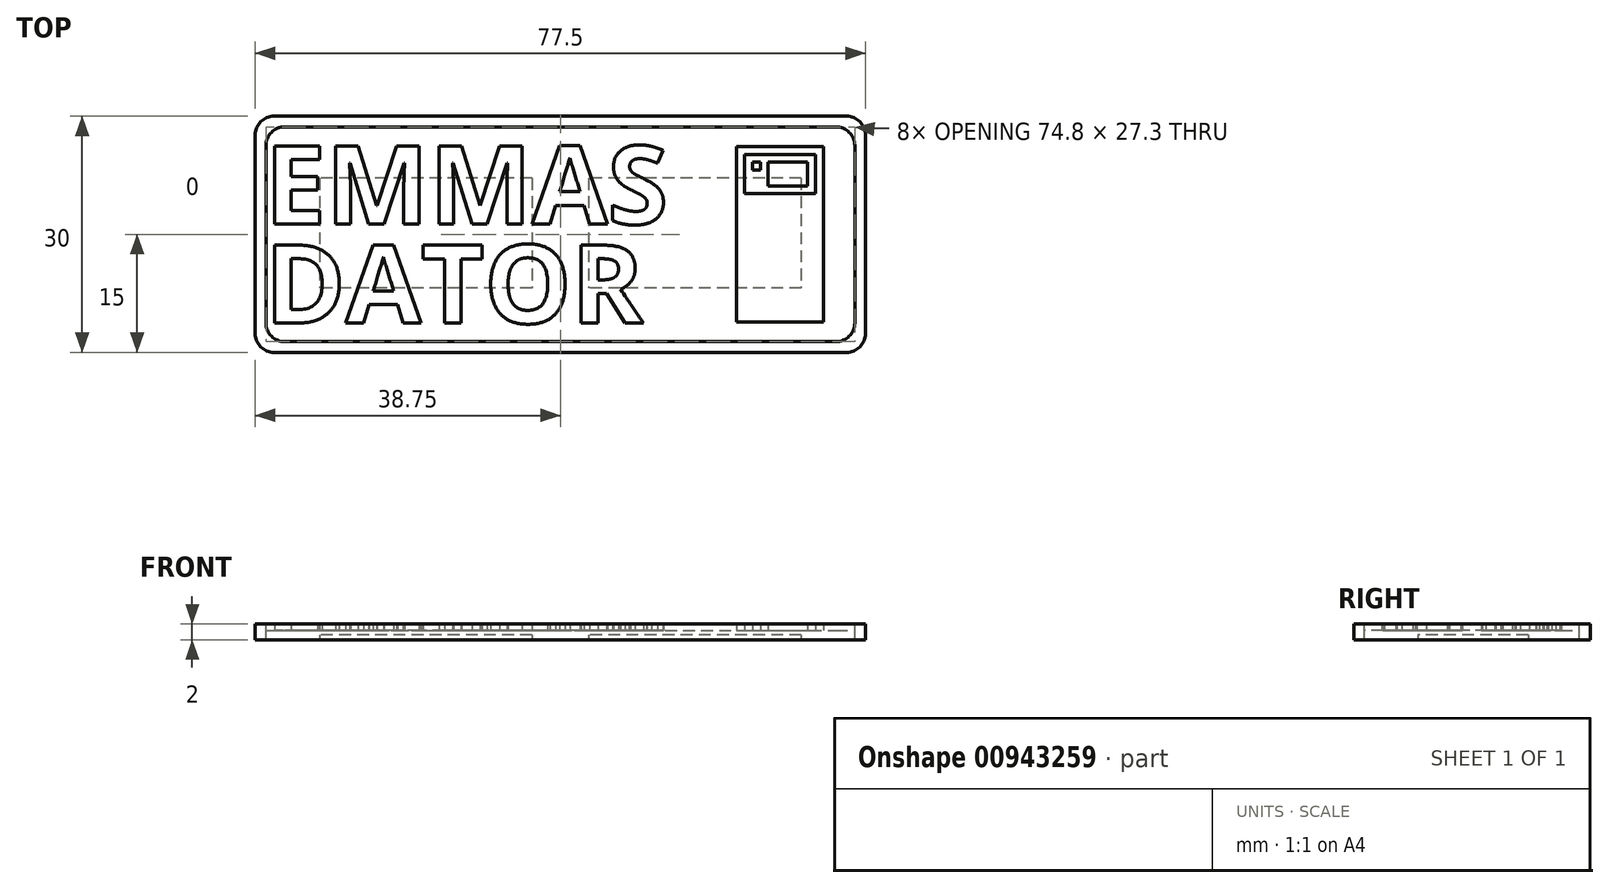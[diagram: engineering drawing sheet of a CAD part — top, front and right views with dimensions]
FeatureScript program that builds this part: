
annotation { "Feature Type Name" : "Feature", "Feature Type Description" : "" }
export const myFeature = defineFeature(function(context is Context, id is Id, definition is map)
    precondition{}
    {
        {
            var Q0;
            Q0=qCreatedBy(makeId("Top.planeOp"),FACE);
            var sketch = newSketch(context, id + "F0", { "sketchPlane" : qUnion([Q0])});
            skLineSegment(sketch, "E0.bottom", {"start": v(-77.5, 30) * mm, "end": v(0, 30) * mm});
            skLineSegment(sketch, "E0.top", {"start": v(-77.5, 0) * mm, "end": v(0, 0) * mm});
            skLineSegment(sketch, "E0.left", {"start": v(-77.5, 30) * mm, "end": v(-77.5, 0) * mm});
            skLineSegment(sketch, "E0.right", {"start": v(0, 30) * mm, "end": v(0, 0) * mm});
            skSolve(sketch);
        }
        {
            var Q0;
            Q0=makeQuery(id+"F0.imprint","IMPRINT",FACE,{"disambiguationData":[TD([[makeQuery(id+"F0.imprint","IMPRINT",EDGE,{"derivedFrom":sQuery(id+"F0.wireOp",EDGE,"E0.bottom")}),-1.0]])]});
            extrude(context, id + "F1", {"entities" : qUnion([Q0]), "oppositeDirection" : true, "depth" : 2 * mm, "offsetDistance" : 25 * mm});
        }
        {
            var Q0;
            Q0=makeQuery(id+"F1.opExtrude","CAP_FACE",FACE,{"disambiguationData":[OSD([sQuery(id+"F0.wireOp",EDGE,"E0.bottom"),sQuery(id+"F0.wireOp",EDGE,"E0.top"),sQuery(id+"F0.wireOp",EDGE,"E0.left"),sQuery(id+"F0.wireOp",EDGE,"E0.right")])],"isStart":true});
            var sketch = newSketch(context, id + "F2", { "sketchPlane" : qUnion([Q0])});
            skLineSegment(sketch, "E1.bottom", {"start": v(-76.15, 28.65) * mm, "end": v(-1.35, 28.65) * mm});
            skLineSegment(sketch, "E1.top", {"start": v(-76.15, 1.35) * mm, "end": v(-1.35, 1.35) * mm});
            skLineSegment(sketch, "E1.left", {"start": v(-76.15, 28.65) * mm, "end": v(-76.15, 1.35) * mm});
            skLineSegment(sketch, "E1.right", {"start": v(-1.35, 28.65) * mm, "end": v(-1.35, 1.35) * mm});
            skSolve(sketch);
        }
        {
            var Q0;
            Q0=makeQuery(id+"F2.imprint","IMPRINT",FACE,{"disambiguationData":[TD([[makeQuery(id+"F2.imprint","IMPRINT",EDGE,{"derivedFrom":sQuery(id+"F2.wireOp",EDGE,"E1.bottom")}),-1.0]])]});
            extrude(context, id + "F3", {"entities" : qUnion([Q0]), "operationType" : NewBodyOperationType.REMOVE, "oppositeDirection" : true, "depth" : 0.8 * mm, "offsetDistance" : 25 * mm});
        }
        {
            var Q0;
            Q0=makeQuery(id+"F1.opExtrude","SWEPT_EDGE",EDGE,{"disambiguationData":[OSD([sQuery(id+"F0.wireOp",EDGE,"E0.bottom"),sQuery(id+"F0.wireOp",EDGE,"E0.right")])]});
            var Q1;
            Q1=makeQuery(id+"F1.opExtrude","SWEPT_EDGE",EDGE,{"disambiguationData":[OSD([sQuery(id+"F0.wireOp",EDGE,"E0.top"),sQuery(id+"F0.wireOp",EDGE,"E0.right")])]});
            var Q2;
            Q2=makeQuery(id+"F1.opExtrude","SWEPT_EDGE",EDGE,{"disambiguationData":[OSD([sQuery(id+"F0.wireOp",EDGE,"E0.top"),sQuery(id+"F0.wireOp",EDGE,"E0.left")])]});
            var Q3;
            Q3=makeQuery(id+"F1.opExtrude","SWEPT_EDGE",EDGE,{"disambiguationData":[OSD([sQuery(id+"F0.wireOp",EDGE,"E0.bottom"),sQuery(id+"F0.wireOp",EDGE,"E0.left")])]});
            var Q4;
            Q4=makeQuery(id+"F3.boolean.opBoolean","COPY",EDGE,{"derivedFrom":makeQuery(id+"F3.opExtrude","SWEPT_EDGE",EDGE,{"disambiguationData":[OSD([sQuery(id+"F2.wireOp",EDGE,"E1.top"),sQuery(id+"F2.wireOp",EDGE,"E1.right")])]})});
            var Q5;
            Q5=makeQuery(id+"F3.boolean.opBoolean","COPY",EDGE,{"derivedFrom":makeQuery(id+"F3.opExtrude","SWEPT_EDGE",EDGE,{"disambiguationData":[OSD([sQuery(id+"F2.wireOp",EDGE,"E1.bottom"),sQuery(id+"F2.wireOp",EDGE,"E1.right")])]})});
            var Q6;
            Q6=makeQuery(id+"F3.boolean.opBoolean","COPY",EDGE,{"derivedFrom":makeQuery(id+"F3.opExtrude","SWEPT_EDGE",EDGE,{"disambiguationData":[OSD([sQuery(id+"F2.wireOp",EDGE,"E1.bottom"),sQuery(id+"F2.wireOp",EDGE,"E1.left")])]})});
            var Q7;
            Q7=makeQuery(id+"F3.boolean.opBoolean","COPY",EDGE,{"derivedFrom":makeQuery(id+"F3.opExtrude","SWEPT_EDGE",EDGE,{"disambiguationData":[OSD([sQuery(id+"F2.wireOp",EDGE,"E1.top"),sQuery(id+"F2.wireOp",EDGE,"E1.left")])]})});
            fillet(context, id + "F4", {"entities" : qUnion([Q0, Q1, Q2, Q3, Q4, Q5, Q6, Q7]), "radius" : 2.4 * mm, "tangentPropagation" : true, "allowEdgeOverflow" : false});
        }
        {
            var Q0;
            Q0=makeQuery(id+"F3.boolean.opBoolean","COPY",FACE,{"derivedFrom":makeQuery(id+"F3.opExtrude","CAP_FACE",FACE,{"disambiguationData":[OSD([sQuery(id+"F2.wireOp",EDGE,"E1.bottom"),sQuery(id+"F2.wireOp",EDGE,"E1.top"),sQuery(id+"F2.wireOp",EDGE,"E1.left"),sQuery(id+"F2.wireOp",EDGE,"E1.right")])],"isStart":false})});
            extrude(context, id + "F5", {"entities" : qUnion([Q0]), "oppositeDirection" : true, "depth" : 1.2 * mm, "offsetDistance" : 25 * mm});
        }
        {
            var Q0;
            Q0=makeQuery(id+"F5.opExtrude","SWEPT_BODY",BODY,{"disambiguationData":[OSD([sQuery(id+"F2.wireOp",EDGE,"E1.bottom"),sQuery(id+"F2.wireOp",EDGE,"E1.top"),sQuery(id+"F2.wireOp",EDGE,"E1.left"),sQuery(id+"F2.wireOp",EDGE,"E1.right")])]});
            var Q1;
            Q1=makeQuery(id+"F1.opExtrude","SWEPT_BODY",BODY,{"disambiguationData":[OSD([sQuery(id+"F0.wireOp",EDGE,"E0.bottom"),sQuery(id+"F0.wireOp",EDGE,"E0.top"),sQuery(id+"F0.wireOp",EDGE,"E0.left"),sQuery(id+"F0.wireOp",EDGE,"E0.right")])]});
            booleanBodies(context, id + "F6", {"operationType" : BooleanOperationType.SUBTRACTION, "tools" : qUnion([Q0]), "targets" : qUnion([Q1]), "keepTools" : true});
        }
        {
            var Q0;
            Q0=makeQuery(id+"F5.opExtrude","CAP_FACE",FACE,{"disambiguationData":[OSD([sQuery(id+"F2.wireOp",EDGE,"E1.bottom"),sQuery(id+"F2.wireOp",EDGE,"E1.top"),sQuery(id+"F2.wireOp",EDGE,"E1.left"),sQuery(id+"F2.wireOp",EDGE,"E1.right")])],"isStart":true});
            var sketch = newSketch(context, id + "F7", { "sketchPlane" : qUnion([Q0])});
            skText(sketch, "E2", { "text": "EMMAS", "fontName": "OpenSans-Bold.ttf"});
            skText(sketch, "E3", { "text": "DATOR", "fontName": "OpenSans-Bold.ttf"});
            skLineSegment(sketch, "E4.bottom", {"start": v(-16.35, 26.15) * mm, "end": v(-5.35, 26.15) * mm});
            skLineSegment(sketch, "E4.top", {"start": v(-16.35, 3.85) * mm, "end": v(-5.35, 3.85) * mm});
            skLineSegment(sketch, "E4.left", {"start": v(-16.35, 26.15) * mm, "end": v(-16.35, 3.85) * mm});
            skLineSegment(sketch, "E4.right", {"start": v(-5.35, 26.15) * mm, "end": v(-5.35, 3.85) * mm});
            skLineSegment(sketch, "E5.bottom", {"start": v(-15.35, 25.15) * mm, "end": v(-6.35, 25.15) * mm});
            skLineSegment(sketch, "E5.top", {"start": v(-15.35, 20.15) * mm, "end": v(-6.35, 20.15) * mm});
            skLineSegment(sketch, "E5.left", {"start": v(-15.35, 25.15) * mm, "end": v(-15.35, 20.15) * mm});
            skLineSegment(sketch, "E5.right", {"start": v(-6.35, 25.15) * mm, "end": v(-6.35, 20.15) * mm});
            skLineSegment(sketch, "E6.bottom", {"start": v(-14.35, 24.15) * mm, "end": v(-13.35, 24.15) * mm});
            skLineSegment(sketch, "E6.top", {"start": v(-14.35, 23.15) * mm, "end": v(-13.35, 23.15) * mm});
            skLineSegment(sketch, "E6.left", {"start": v(-14.35, 24.15) * mm, "end": v(-14.35, 23.15) * mm});
            skLineSegment(sketch, "E6.right", {"start": v(-13.35, 24.15) * mm, "end": v(-13.35, 23.15) * mm});
            skLineSegment(sketch, "E7.bottom", {"start": v(-12.35, 24.15) * mm, "end": v(-7.35, 24.15) * mm});
            skLineSegment(sketch, "E7.top", {"start": v(-12.35, 21.15) * mm, "end": v(-7.35, 21.15) * mm});
            skLineSegment(sketch, "E7.left", {"start": v(-12.35, 24.15) * mm, "end": v(-12.35, 21.15) * mm});
            skLineSegment(sketch, "E7.right", {"start": v(-7.35, 24.15) * mm, "end": v(-7.35, 21.15) * mm});
            const initialGuessF7  = {"E2": [-0.0763, 0.0163, 1, 0, 0.01], "E3": [-0.0763, 0.0037, 1, 0, 0.01]};
            skSetInitialGuess(sketch, initialGuessF7);
            skSolve(sketch);
        }
        {
            var Q0;
            Q0 = qSketchRegion(id + "F7", true);
            var Q1;
            Q1=makeQuery(id+"F7.imprint","IMPRINT",FACE,{"disambiguationData":[TD([[makeQuery(id+"F7.imprint","IMPRINT",EDGE,{"derivedFrom":sQuery(id+"F7.wireOp",EDGE,"E7.bottom")}),-1.0]])]});
            var Q2;
            Q2=makeQuery(id+"F7.imprint","IMPRINT",FACE,{"disambiguationData":[TD([[makeQuery(id+"F7.imprint","IMPRINT",EDGE,{"derivedFrom":sQuery(id+"F7.wireOp",EDGE,"E6.bottom")}),-1.0]])]});
            extrude(context, id + "F8", {"entities" : qUnion([Q0, Q1, Q2]), "operationType" : NewBodyOperationType.ADD, "depth" : 0.8 * mm, "offsetDistance" : 25 * mm});
        }
        {
            var Q0;
            Q0=makeQuery(id+"F5.opExtrude","CAP_FACE",FACE,{"disambiguationData":[OSD([sQuery(id+"F2.wireOp",EDGE,"E1.bottom"),sQuery(id+"F2.wireOp",EDGE,"E1.top"),sQuery(id+"F2.wireOp",EDGE,"E1.left"),sQuery(id+"F2.wireOp",EDGE,"E1.right")])],"isStart":false});
            var sketch = newSketch(context, id + "F9", { "sketchPlane" : qUnion([Q0])});
            skLineSegment(sketch, "E8.bottom", {"start": v(-8.15, -22.15) * mm, "end": v(-35.15, -22.15) * mm});
            skLineSegment(sketch, "E8.top", {"start": v(-8.15, -8.15) * mm, "end": v(-35.15, -8.15) * mm});
            skLineSegment(sketch, "E8.left", {"start": v(-8.15, -22.15) * mm, "end": v(-8.15, -8.15) * mm});
            skLineSegment(sketch, "E8.right", {"start": v(-35.15, -22.15) * mm, "end": v(-35.15, -8.15) * mm});
            skLineSegment(sketch, "E9.bottom", {"start": v(-42.35, -22.15) * mm, "end": v(-69.35, -22.15) * mm});
            skLineSegment(sketch, "E9.top", {"start": v(-42.35, -8.15) * mm, "end": v(-69.35, -8.15) * mm});
            skLineSegment(sketch, "E9.left", {"start": v(-42.35, -22.15) * mm, "end": v(-42.35, -8.15) * mm});
            skLineSegment(sketch, "E9.right", {"start": v(-69.35, -22.15) * mm, "end": v(-69.35, -8.15) * mm});
            skSolve(sketch);
        }
        {
            var Q0;
            Q0 = qSketchRegion(id + "F9", true);
            extrude(context, id + "F10", {"entities" : qUnion([Q0]), "operationType" : NewBodyOperationType.REMOVE, "oppositeDirection" : true, "depth" : 0.6 * mm, "offsetDistance" : 25 * mm});
        }
    });
